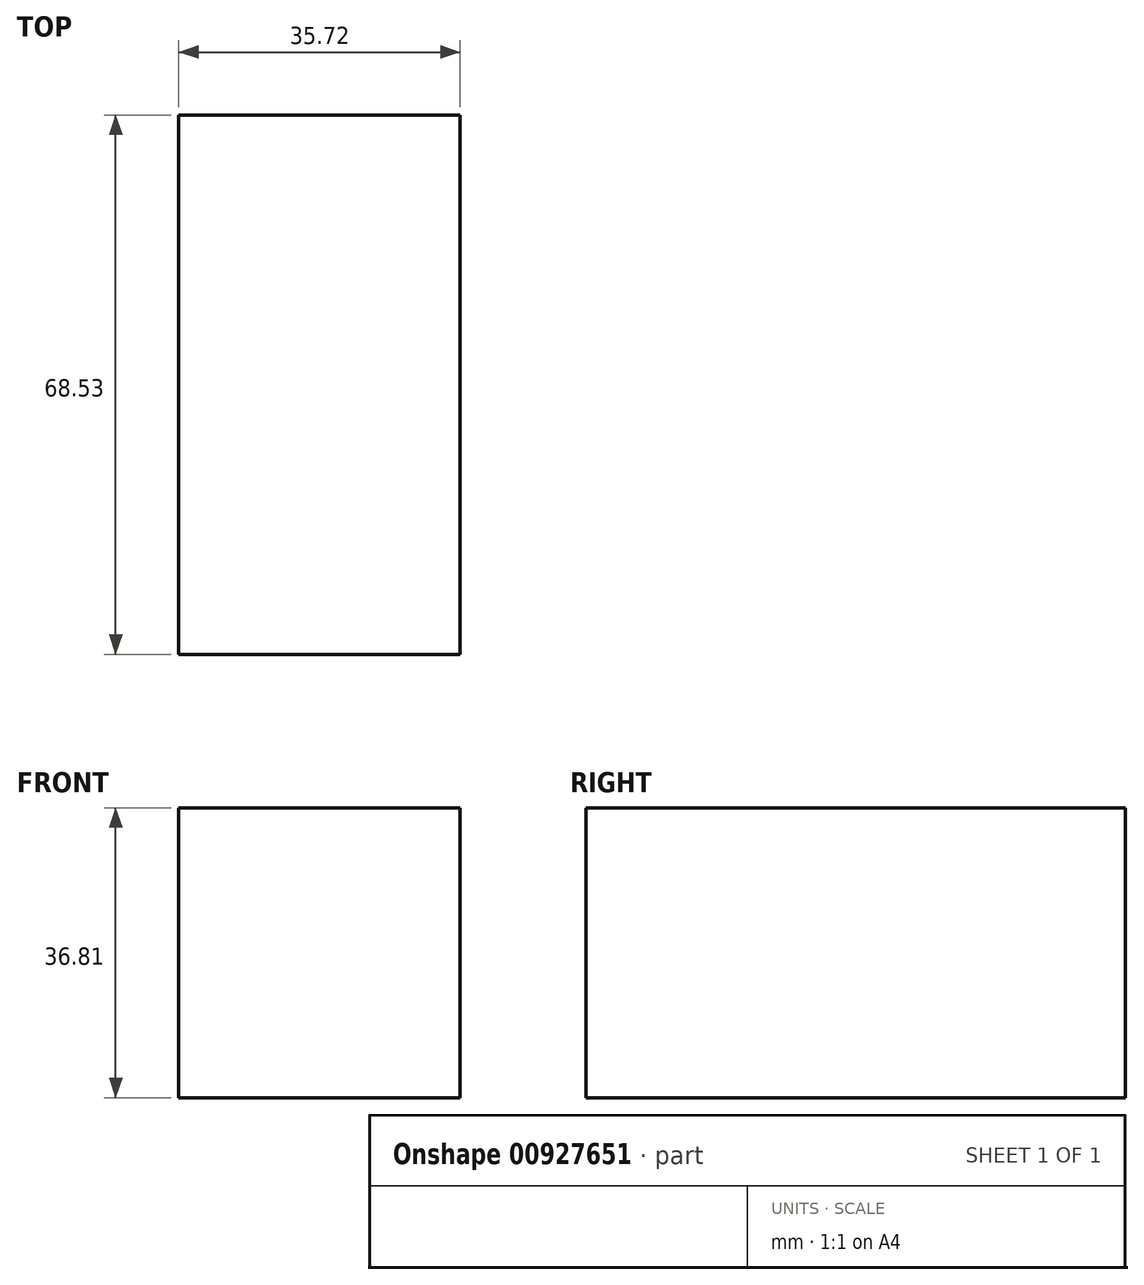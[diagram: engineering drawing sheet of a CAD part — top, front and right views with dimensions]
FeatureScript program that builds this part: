
annotation { "Feature Type Name" : "Feature", "Feature Type Description" : "" }
export const myFeature = defineFeature(function(context is Context, id is Id, definition is map)
    precondition{}
    {
        {
            var Q0;
            Q0=qCreatedBy(makeId("Top.planeOp"),FACE);
            var sketch = newSketch(context, id + "F0", { "sketchPlane" : qUnion([Q0])});
            skLineSegment(sketch, "E0.bottom", {"start": v(-21.92, -21.14) * mm, "end": v(13.8, -21.14) * mm});
            skLineSegment(sketch, "E0.top", {"start": v(-21.92, 47.39) * mm, "end": v(13.8, 47.39) * mm});
            skLineSegment(sketch, "E0.left", {"start": v(-21.92, -21.14) * mm, "end": v(-21.92, 47.39) * mm});
            skLineSegment(sketch, "E0.right", {"start": v(13.8, -21.14) * mm, "end": v(13.8, 47.39) * mm});
            skSolve(sketch);
        }
        {
            var Q0;
            Q0 = qSketchRegion(id + "F0", true);
            extrude(context, id + "F1", {"entities" : qUnion([Q0]), "depth" : 36.81 * mm, "offsetDistance" : 25.4 * mm});
        }
    });
